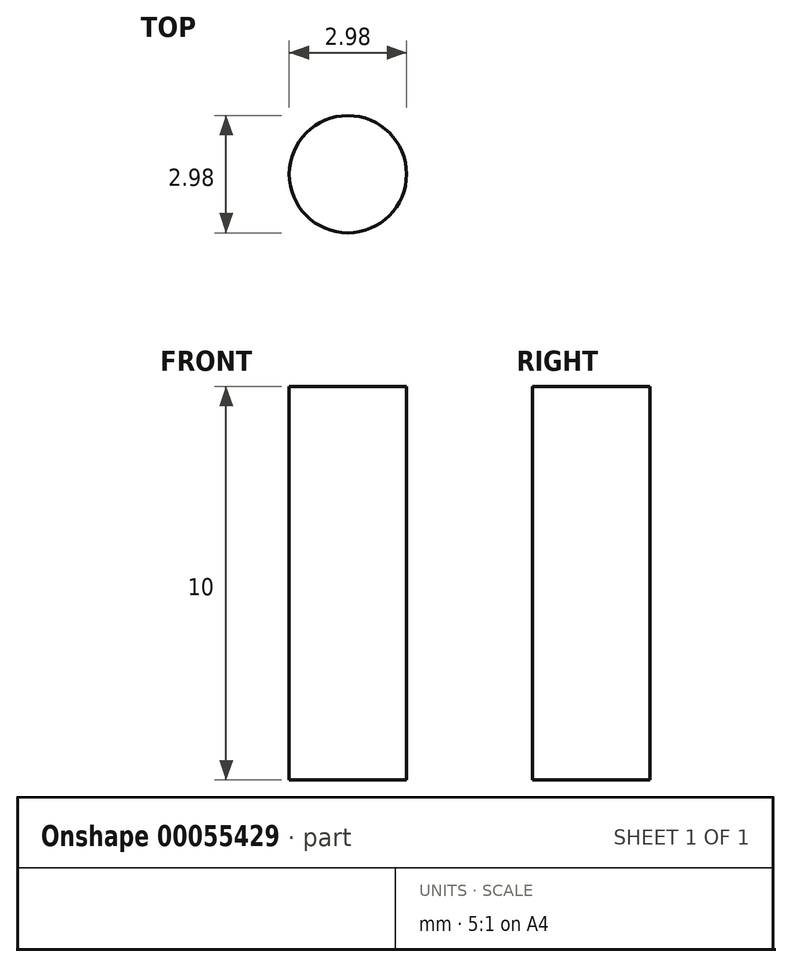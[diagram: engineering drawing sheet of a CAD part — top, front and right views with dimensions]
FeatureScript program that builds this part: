
annotation { "Feature Type Name" : "Feature", "Feature Type Description" : "" }
export const myFeature = defineFeature(function(context is Context, id is Id, definition is map)
    precondition{}
    {
        {
            var Q0;
            Q0=qCreatedBy(makeId("Top.planeOp"),FACE);
            var sketch = newSketch(context, id + "F0", { "sketchPlane" : qUnion([Q0])});
            skCircle(sketch, "E0", {"center": v(0, 0) * mm, "radius": 1.5 * mm});
            skSolve(sketch);
        }
        {
            var Q0;
            Q0=makeQuery(id+"F0.imprint","IMPRINT",FACE,{"disambiguationData":[TD([[makeQuery(id+"F0.imprint","IMPRINT",EDGE,{"derivedFrom":sQuery(id+"F0.wireOp",EDGE,"E0")}),1.0]])]});
            extrude(context, id + "F1", {"entities" : qUnion([Q0]), "depth" : 10 * mm});
        }
    });
